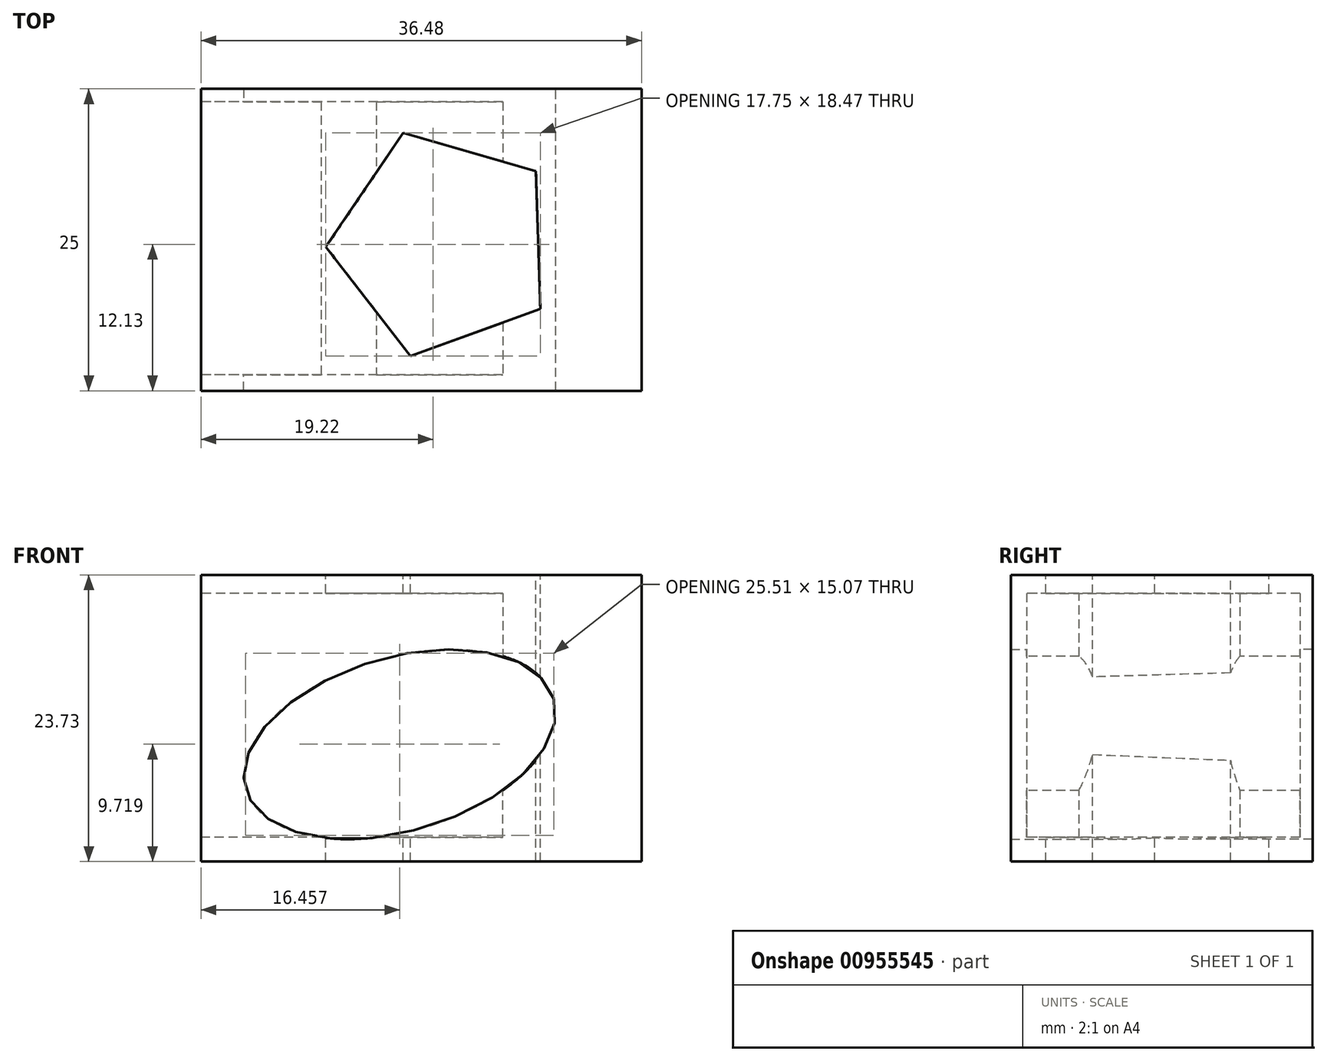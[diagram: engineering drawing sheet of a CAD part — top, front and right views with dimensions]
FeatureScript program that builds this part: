
annotation { "Feature Type Name" : "Feature", "Feature Type Description" : "" }
export const myFeature = defineFeature(function(context is Context, id is Id, definition is map)
    precondition{}
    {
        {
            var Q0;
            Q0=qCreatedBy(makeId("Front.planeOp"),FACE);
            var sketch = newSketch(context, id + "F0", { "sketchPlane" : qUnion([Q0])});
            skLineSegment(sketch, "E0.bottom", {"start": v(36.48, 23.73) * mm, "end": v(0, 23.73) * mm});
            skLineSegment(sketch, "E0.top", {"start": v(36.48, 0) * mm, "end": v(0, 0) * mm});
            skLineSegment(sketch, "E0.left", {"start": v(36.48, 23.73) * mm, "end": v(36.48, 0) * mm});
            skLineSegment(sketch, "E0.right", {"start": v(0, 23.73) * mm, "end": v(0, 0) * mm});
            skSolve(sketch);
        }
        {
            var Q0;
            Q0 = qSketchRegion(id + "F0", true);
            extrude(context, id + "F1", {"entities" : qUnion([Q0]), "depth" : 25 * mm, "offsetDistance" : 25 * mm});
        }
        {
            var Q0;
            Q0=makeQuery(id+"F1.opExtrude","CAP_FACE",FACE,{"disambiguationData":[OSD([sQuery(id+"F0.wireOp",EDGE,"E0.bottom"),sQuery(id+"F0.wireOp",EDGE,"E0.top"),sQuery(id+"F0.wireOp",EDGE,"E0.left"),sQuery(id+"F0.wireOp",EDGE,"E0.right")])],"isStart":false});
            var sketch = newSketch(context, id + "F2", { "sketchPlane" : qUnion([Q0])});
            skEllipse(sketch, "E1", {"center": v(16.46, 9.72) * mm, "majorRadius": 13.3 * mm, "minorRadius": 7.2 * mm, "majorAxis": v(0.96, 0.28)});
            skSolve(sketch);
        }
        {
            var Q0;
            Q0=makeQuery(id+"F2.imprint","IMPRINT",FACE,{"disambiguationData":[TD([[makeQuery(id+"F2.imprint","IMPRINT",EDGE,{"derivedFrom":sQuery(id+"F2.wireOp",EDGE,"E1")}),1.0]])]});
            extrude(context, id + "F3", {"entities" : qUnion([Q0]), "operationType" : NewBodyOperationType.REMOVE, "oppositeDirection" : true, "depth" : 25 * mm, "offsetDistance" : 25 * mm});
        }
        {
            var Q0;
            Q0=makeQuery(id+"F1.opExtrude","SWEPT_FACE",FACE,{"disambiguationData":[OSD([sQuery(id+"F0.wireOp",EDGE,"E0.bottom")])]});
            var sketch = newSketch(context, id + "F4", { "sketchPlane" : qUnion([Q0])});
            skCircle(sketch, "E2.cCircle", {"center": v(20.06, -12.77) * mm, "radius": 7.86 * mm, "construction": true});
            skLineSegment(sketch, "E2.0", {"start": v(10.34, -13.08) * mm, "end": v(16.76, -3.63) * mm});
            skLineSegment(sketch, "E2.1", {"start": v(16.76, -3.63) * mm, "end": v(27.73, -6.81) * mm});
            skLineSegment(sketch, "E2.2", {"start": v(27.73, -6.81) * mm, "end": v(28.1, -18.23) * mm});
            skLineSegment(sketch, "E2.3", {"start": v(28.1, -18.23) * mm, "end": v(17.35, -22.1) * mm});
            skLineSegment(sketch, "E2.4", {"start": v(17.35, -22.1) * mm, "end": v(10.34, -13.08) * mm});
            skPoint(sketch, "E2.0.midPoint", {"position": v(13.55, -8.36) * mm});
            skSolve(sketch);
        }
        {
            var Q0;
            Q0 = qSketchRegion(id + "F4", true);
            extrude(context, id + "F5", {"entities" : qUnion([Q0]), "operationType" : NewBodyOperationType.REMOVE, "oppositeDirection" : true, "depth" : 25 * mm, "offsetDistance" : 25 * mm});
        }
        {
            var Q0;
            Q0=makeQuery(id+"F1.opExtrude","SWEPT_FACE",FACE,{"disambiguationData":[OSD([sQuery(id+"F0.wireOp",EDGE,"E0.right")])]});
            var sketch = newSketch(context, id + "F6", { "sketchPlane" : qUnion([Q0])});
            skLineSegment(sketch, "E3.bottom", {"start": v(1.07, 22.22) * mm, "end": v(23.68, 22.22) * mm});
            skLineSegment(sketch, "E3.top", {"start": v(1.07, 2) * mm, "end": v(23.68, 2) * mm});
            skLineSegment(sketch, "E3.left", {"start": v(1.07, 22.22) * mm, "end": v(1.07, 2) * mm});
            skLineSegment(sketch, "E3.right", {"start": v(23.68, 22.22) * mm, "end": v(23.68, 2) * mm});
            skSolve(sketch);
        }
        {
            var Q0;
            Q0 = qSketchRegion(id + "F6", true);
            extrude(context, id + "F7", {"entities" : qUnion([Q0]), "operationType" : NewBodyOperationType.REMOVE, "oppositeDirection" : true, "depth" : 25 * mm, "offsetDistance" : 25 * mm});
        }
    });
